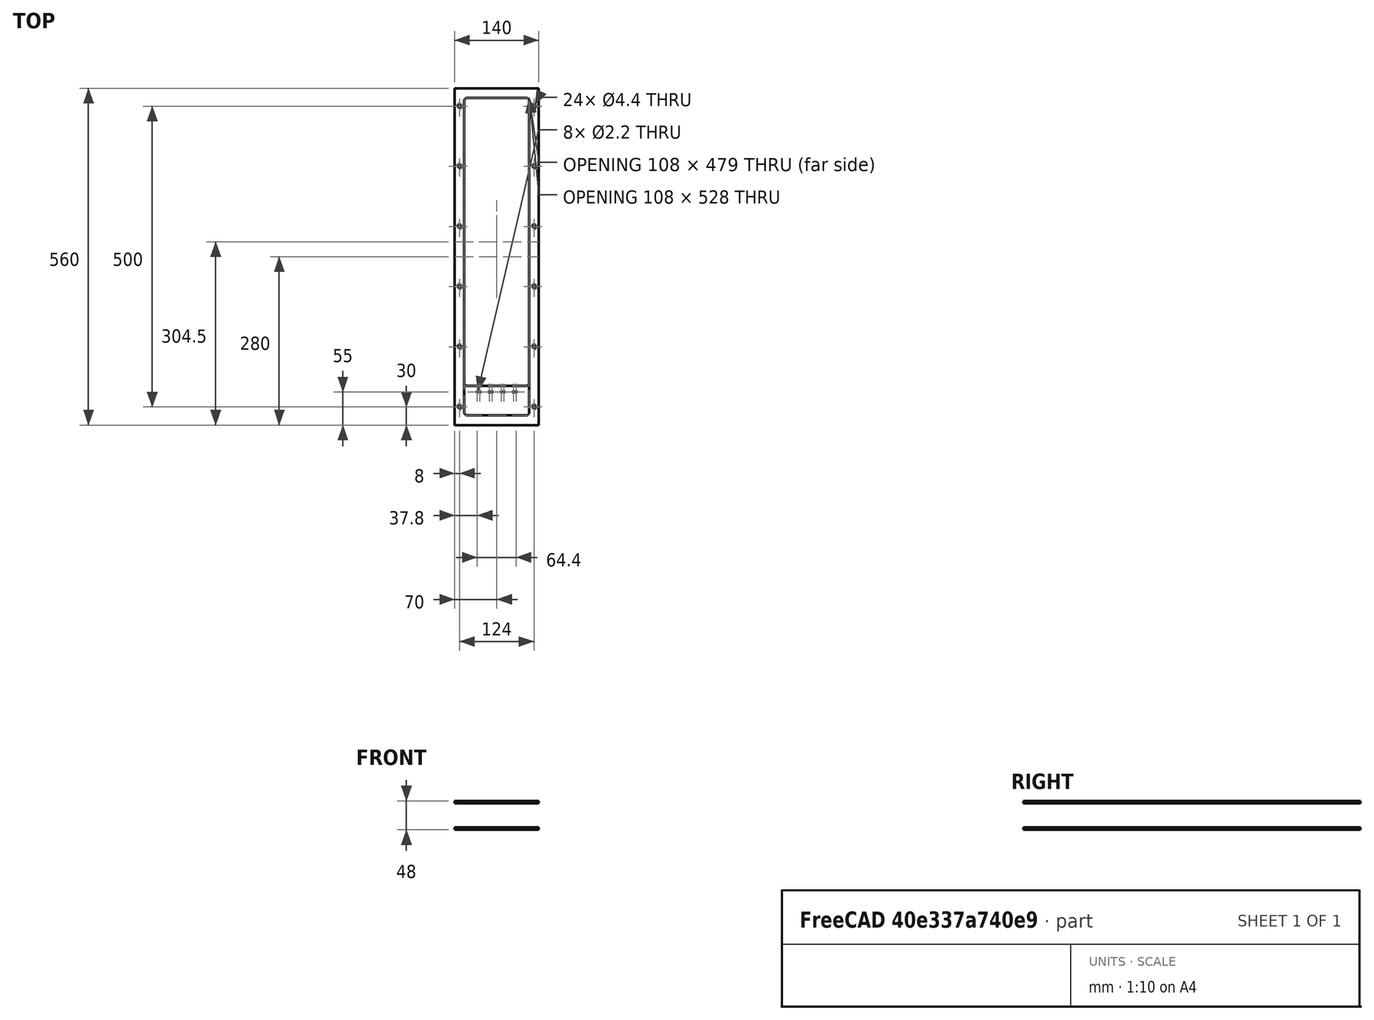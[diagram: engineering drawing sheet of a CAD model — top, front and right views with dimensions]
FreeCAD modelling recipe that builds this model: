
FCSTD DOCUMENT  (FreeCAD 0.20R29177 +233 (Git))
Label: carrier_plate_v1-0-560
License: All rights reserved
LicenseURL: http://en.wikipedia.org/wiki/All_rights_reserved
objects: TechDraw::DrawViewDimension×24, Sketcher::SketchObject×6, PartDesign::Pocket×4, PartDesign::Body×4, PartDesign::Pad×3, TechDraw::DrawViewBalloon×3, PartDesign::LinearPattern×2, PartDesign::FeatureBase×2, TechDraw::DrawViewPart×2, Spreadsheet::Sheet×1, TechDraw::DrawSVGTemplate×1, PartDesign::Chamfer×1, Part::Refine×1, PartDesign::Mirrored×1, TechDraw::DrawPage×1
note: 32 computed .brp shape members not serialized (recipe doc carries the construction recipe); baked Part::Feature solids carry a one-line shape summary decoded from their .brp

FEATURE [Sketcher::SketchObject] Sketch
  FullyConstrained = true
  MapMode = 5
  Support = -> [XY_Plane]
  expr: Constraints[10] = <<parameters>>.baseplate_length
  expr: Constraints[27] = <<parameters>>.side_width
  expr: Constraints[28] = <<parameters>>.side_width
  expr: Constraints[41] = <<parameters>>.cooling_fin_x_shift
  expr: Constraints[9] = <<parameters>>.baseplate_width
  sketch-geometry (20):
    g0: LineSegment StartX=-70 StartY=0 StartZ=0 EndX=70 EndY=0 EndZ=0
    g1: LineSegment StartX=70 StartY=0 StartZ=0 EndX=70 EndY=560 EndZ=0
    g2: LineSegment StartX=70 StartY=560 StartZ=0 EndX=-70 EndY=560 EndZ=0
    g3: LineSegment StartX=-70 StartY=560 StartZ=0 EndX=-70 EndY=0 EndZ=0
    g4: LineSegment StartX=-49 StartY=544 StartZ=0 EndX=49 EndY=544 EndZ=0
    g5: LineSegment StartX=54 StartY=539 StartZ=0 EndX=54 EndY=70 EndZ=0
    g6: LineSegment StartX=49 StartY=65 StartZ=0 EndX=-49 EndY=65 EndZ=0
    g7: LineSegment StartX=-54 StartY=70 StartZ=0 EndX=-54 EndY=539 EndZ=0
    g8: ArcOfCircle CenterX=49 CenterY=539 CenterZ=0 NormalX=0 NormalY=0 NormalZ=1 AngleXU=0 Radius=5 StartAngle=-3.0065e-12 EndAngle=1.5708
    g9: ArcOfCircle CenterX=-49 CenterY=539 CenterZ=0 NormalX=0 NormalY=0 NormalZ=1 AngleXU=0 Radius=5 StartAngle=1.5708 EndAngle=3.14159
    g10: ArcOfCircle CenterX=49 CenterY=70 CenterZ=0 NormalX=0 NormalY=0 NormalZ=1 AngleXU=0 Radius=5 StartAngle=4.71239 EndAngle=6.28319
    g11: ArcOfCircle CenterX=-49 CenterY=70 CenterZ=0 NormalX=0 NormalY=0 NormalZ=1 AngleXU=0 Radius=5 StartAngle=3.14159 EndAngle=4.71239
    g12: LineSegment StartX=-42.19 StartY=42 StartZ=0 EndX=59.31 EndY=42 EndZ=0
    g13: LineSegment StartX=59.31 StartY=42 StartZ=0 EndX=59.31 EndY=59 EndZ=0
    g14: LineSegment StartX=59.31 StartY=59 StartZ=0 EndX=-42.19 EndY=59 EndZ=0
    g15: LineSegment StartX=-42.19 StartY=59 StartZ=0 EndX=-42.19 EndY=42 EndZ=0
    g16: GeomPoint X=8.56 Y=50.5 Z=0
    g17: Circle CenterX=-22.19 CenterY=45 CenterZ=0 NormalX=0 NormalY=0 NormalZ=1 AngleXU=0 Radius=1.5
    g18: Circle CenterX=37.81 CenterY=45 CenterZ=0 NormalX=0 NormalY=0 NormalZ=1 AngleXU=0 Radius=1.5
    g19: LineSegment StartX=-22.19 StartY=45 StartZ=0 EndX=37.81 EndY=45 EndZ=0
  constraints (52):
    c: Coincident(g0,g1)
    c: Coincident(g1,g2)
    c: Coincident(g2,g3)
    c: Coincident(g3,g0)
    c: Horizontal(g0)
    c: Horizontal(g2)
    c: Vertical(g1)
    c: Vertical(g3)
    c: Symmetric(g0,g0,g-1)
    c: DistanceX(g0,g0) = 140
    c: DistanceY(g3,g3) = 560
    c: Horizontal(g6)
    c: Vertical(g5)
    c: Vertical(g7)
    c: Tangent(g5,g8) = 1.5708
    c: Tangent(g4,g8) = 1.5708
    c: Tangent(g7,g9) = 1.5708
    c: Tangent(g4,g9) = 1.5708
    c: Tangent(g6,g10) = 1.5708
    c: Tangent(g5,g10) = 1.5708
    c: Tangent(g6,g11) = 1.5708
    c: Tangent(g7,g11) = 1.5708
    c: Equal(g10,g11)
    c: Equal(g11,g8)
    c: Equal(g8,g9)
    c: Radius(g8) = 5
    c: Symmetric(g9,g8,g-2)
    c: DistanceY(g4,g1) = 16
    c: DistanceX(g5,g1) = 16
    c: DistanceY(g0,g6) = 65
    c: Coincident(g12,g13)
    c: Coincident(g13,g14)
    c: Coincident(g14,g15)
    c: Coincident(g15,g12)
    c: Horizontal(g12)
    c: Horizontal(g14)
    c: Vertical(g13)
    c: Vertical(g15)
    c: DistanceY(g13,g13) = 17
    c: Symmetric(g14,g12,g16)
    c: DistanceX(g12,g12) = 101.5
    c: DistanceX(g-1,g16) = 8.56
    c: Coincident(g19,g17)
    c: Coincident(g19,g18)
    c: Horizontal(g19)
    c: Equal(g18,g17)
    c: Diameter(g18) = 3
    c: DistanceY(g12,g17) = 3
    c: DistanceY(g0,g12) = 42
    c: DistanceX(g19,g19) = 60
    c: DistanceX(g12,g17) = 20
    c: DistanceY(g12,g6) = 23
FEATURE [PartDesign::Pad] Pad
  Direction = (0,0,1)
  Length = 4
  Length2 = 100
  Profile = -> Sketch
  Reversed = true
  Type = 0
  expr: Length = <<parameters>>.baseplate_thickness
FEATURE [Spreadsheet::Sheet] Spreadsheet  label="parameters"
  cells = B1=frame dimnsions:; B2=baseplate width; C2(baseplate_width)==140mm; D2=cooling fin x shift; E2(cooling_fin_x_shift)==8.56mm; B3=baseplate length; C3(baseplate_length)==560mm; D3=plate space; E3(plate_space)==40mm; B4=side width; C4(side_width)==16mm; B5=baseplate thickness; C5(baseplate_thickness)==4mm; B6=frame holes:; B7=hole step; C7(hole_step)==100mm; B8=hole offset; C8(hole_offset)==30mm
FEATURE [Sketcher::SketchObject] Sketch001
  FullyConstrained = true
  MapMode = 5
  Support = -> [Pad]
  expr: Constraints[3] = <<parameters>>.baseplate_width - <<parameters>>.side_width
  sketch-geometry (2):
    g0: Circle CenterX=62 CenterY=30 CenterZ=0 NormalX=0 NormalY=0 NormalZ=1 AngleXU=0 Radius=2.2
    g1: Circle CenterX=-62 CenterY=30 CenterZ=0 NormalX=0 NormalY=0 NormalZ=1 AngleXU=0 Radius=2.2
  constraints (5):
    c: Symmetric(g1,g0,g-2)
    c: Equal(g1,g0)
    c: Diameter(g0) = 4.4
    c: DistanceX(g1,g0) = 124
    c: DistanceY(g-1,g0) = 30
FEATURE [PartDesign::Pocket] Pocket
  BaseFeature = -> Pad
  Direction = (0,0,-1)
  Length = 5
  Length2 = 100
  Profile = -> Sketch001
  Type = 1
FEATURE [PartDesign::LinearPattern] LinearPattern
  BaseFeature = -> Pocket
  Direction = -> Y_Axis
  Length = 500
  Occurrences = 6
  Originals = -> [Pocket]
  expr: Length = <<parameters>>.baseplate_length - <<parameters>>.hole_offset * 2
  expr: Occurrences = Length / <<parameters>>.hole_step + 1
FEATURE [Sketcher::SketchObject] Sketch002
  FullyConstrained = true
  MapMode = 5
  Support = -> [XY_Plane001]
  expr: Constraints[10] = <<parameters>>.baseplate_length
  expr: Constraints[27] = <<parameters>>.side_width
  expr: Constraints[28] = <<parameters>>.side_width
  expr: Constraints[29] = <<parameters>>.side_width
  expr: Constraints[9] = <<parameters>>.baseplate_width
  sketch-geometry (12):
    g0: LineSegment StartX=-70 StartY=0 StartZ=0 EndX=70 EndY=0 EndZ=0
    g1: LineSegment StartX=70 StartY=0 StartZ=0 EndX=70 EndY=560 EndZ=0
    g2: LineSegment StartX=70 StartY=560 StartZ=0 EndX=-70 EndY=560 EndZ=0
    g3: LineSegment StartX=-70 StartY=560 StartZ=0 EndX=-70 EndY=0 EndZ=0
    g4: LineSegment StartX=-49 StartY=544 StartZ=0 EndX=49 EndY=544 EndZ=0
    g5: LineSegment StartX=54 StartY=539 StartZ=0 EndX=54 EndY=21 EndZ=0
    g6: LineSegment StartX=49 StartY=16 StartZ=0 EndX=-49 EndY=16 EndZ=0
    g7: LineSegment StartX=-54 StartY=21 StartZ=0 EndX=-54 EndY=539 EndZ=0
    g8: ArcOfCircle CenterX=49 CenterY=539 CenterZ=0 NormalX=0 NormalY=0 NormalZ=1 AngleXU=0 Radius=5 StartAngle=1.1e-15 EndAngle=1.5708
    g9: ArcOfCircle CenterX=-49 CenterY=539 CenterZ=0 NormalX=0 NormalY=0 NormalZ=1 AngleXU=0 Radius=5 StartAngle=1.5708 EndAngle=3.14159
    g10: ArcOfCircle CenterX=49 CenterY=21 CenterZ=0 NormalX=0 NormalY=0 NormalZ=1 AngleXU=0 Radius=5 StartAngle=4.71239 EndAngle=6.28319
    g11: ArcOfCircle CenterX=-49 CenterY=21 CenterZ=0 NormalX=0 NormalY=0 NormalZ=1 AngleXU=0 Radius=5 StartAngle=3.14159 EndAngle=4.71239
  constraints (30):
    c: Coincident(g0,g1)
    c: Coincident(g1,g2)
    c: Coincident(g2,g3)
    c: Coincident(g3,g0)
    c: Horizontal(g0)
    c: Horizontal(g2)
    c: Vertical(g1)
    c: Vertical(g3)
    c: Symmetric(g0,g0,g-1)
    c: DistanceX(g0,g0) = 140
    c: DistanceY(g3,g3) = 560
    c: Horizontal(g6)
    c: Vertical(g5)
    c: Vertical(g7)
    c: Tangent(g5,g8) = 1.5708
    c: Tangent(g4,g8) = 1.5708
    c: Tangent(g7,g9) = 1.5708
    c: Tangent(g4,g9) = 1.5708
    c: Tangent(g6,g10) = 1.5708
    c: Tangent(g5,g10) = 1.5708
    c: Tangent(g6,g11) = 1.5708
    c: Tangent(g7,g11) = 1.5708
    c: Equal(g11,g10)
    c: Equal(g10,g8)
    c: Equal(g8,g9)
    c: Radius(g8) = 5
    c: Symmetric(g5,g7,g-2)
    c: DistanceY(g4,g1) = 16
    c: DistanceX(g5,g1) = 16
    c: DistanceY(g0,g6) = 16
FEATURE [PartDesign::Pad] Pad001
  Direction = (0,0,1)
  Length = 4
  Length2 = 100
  Profile = -> Sketch002
  Type = 0
  expr: Length = <<parameters>>.baseplate_thickness
FEATURE [Sketcher::SketchObject] Sketch003
  FullyConstrained = true
  MapMode = 5
  Placement = pos=(0,0,4) rot=(0,0,1;0rad)
  Support = -> [Pad001]
  expr: Constraints[3] = <<parameters>>.baseplate_width - <<parameters>>.side_width
  expr: Constraints[4] = <<parameters>>.hole_offset
  sketch-geometry (2):
    g0: Circle CenterX=62 CenterY=30 CenterZ=0 NormalX=0 NormalY=0 NormalZ=1 AngleXU=0 Radius=2.2
    g1: Circle CenterX=-62 CenterY=30 CenterZ=0 NormalX=0 NormalY=0 NormalZ=1 AngleXU=0 Radius=2.2
  constraints (5):
    c: Symmetric(g1,g0,g-2)
    c: Equal(g0,g1)
    c: Diameter(g0) = 4.4
    c: DistanceX(g1,g0) = 124
    c: DistanceY(g-1,g1) = 30
FEATURE [PartDesign::Pocket] Pocket001
  BaseFeature = -> Pad001
  Direction = (1,1,1)
  Length = 5
  Length2 = 100
  Profile = -> Sketch003
  Type = 1
FEATURE [PartDesign::LinearPattern] LinearPattern001
  BaseFeature = -> Pocket001
  Direction = -> Y_Axis001
  Length = 500
  Occurrences = 6
  Originals = -> [Pocket001]
  expr: Length = <<parameters>>.baseplate_length - 2 * <<parameters>>.hole_offset
  expr: Occurrences = Length / <<parameters>>.hole_step + 1
FEATURE [PartDesign::Body] Body001  label="top_plate"
  Group = -> [Sketch002,Pad001,Sketch003,Pocket001,LinearPattern001]
  Origin = -> Origin001
  Placement = pos=(0,0,40) rot=(0,0,1;0rad)
  Tip = -> LinearPattern001
  expr: .Placement.Base.z = <<parameters>>.plate_space
FEATURE [TechDraw::DrawSVGTemplate] Template
  Height = 297
  Orientation = 1
  Width = 420
FEATURE [Sketcher::SketchObject] Sketch004
  FullyConstrained = true
  MapMode = 5
  Support = -> [LinearPattern]
  sketch-geometry (8):
    g0: LineSegment StartX=-44 StartY=14 StartZ=0 EndX=44 EndY=14 EndZ=0
    g1: LineSegment StartX=44 StartY=14 StartZ=0 EndX=44 EndY=36 EndZ=0
    g2: LineSegment StartX=44 StartY=36 StartZ=0 EndX=-44 EndY=36 EndZ=0
    g3: LineSegment StartX=-44 StartY=36 StartZ=0 EndX=-44 EndY=14 EndZ=0
    g4: Circle CenterX=44 CenterY=36 CenterZ=0 NormalX=0 NormalY=0 NormalZ=1 AngleXU=0 Radius=1.6
    g5: Circle CenterX=-44 CenterY=36 CenterZ=0 NormalX=0 NormalY=0 NormalZ=1 AngleXU=0 Radius=1.6
    g6: Circle CenterX=-44 CenterY=14 CenterZ=0 NormalX=0 NormalY=0 NormalZ=1 AngleXU=0 Radius=1.6
    g7: Circle CenterX=44 CenterY=14 CenterZ=0 NormalX=0 NormalY=0 NormalZ=1 AngleXU=0 Radius=1.6
  constraints (19):
    c: Coincident(g0,g1)
    c: Coincident(g1,g2)
    c: Coincident(g2,g3)
    c: Coincident(g3,g0)
    c: Horizontal(g0)
    c: Vertical(g1)
    c: Vertical(g3)
    c: Symmetric(g1,g2,g-2)
    c: Coincident(g4,g1)
    c: Coincident(g5,g2)
    c: Coincident(g6,g0)
    c: Coincident(g7,g0)
    c: Equal(g7,g4)
    c: Equal(g4,g6)
    c: Equal(g6,g5)
    c: Diameter(g5) = 3.2
    c: DistanceY(g3,g3) = 22
    c: DistanceX(g0,g0) = 88
    c: DistanceY(g7) = 14
FEATURE [PartDesign::Pocket] Pocket002
  BaseFeature = -> LinearPattern
  Direction = (0,0,-1)
  Length = 5
  Length2 = 100
  Profile = -> Sketch004
  Type = 1
FEATURE [PartDesign::Body] Body  label="bottom_plate"
  Group = -> [Sketch,Pad,Sketch001,Pocket,LinearPattern,Sketch004,Pocket002]
  Origin = -> Origin
  Tip = -> Pocket002
FEATURE [PartDesign::FeatureBase] Clone
  BaseFeature = -> Body
FEATURE [PartDesign::Pad] Pad002
  BaseFeature = -> Clone
  Direction = (0,0,1)
  Length = 4
  Length2 = 10
  Profile = -> Clone [Edge19,Edge20,Edge18,Edge16,Edge14,Edge13]
  Reversed = true
  Type = 0
FEATURE [PartDesign::Chamfer] Chamfer
  Angle = 45
  Base = -> Pad002 [Edge48,Edge39,Edge42,Edge49,Edge50,Edge44,Edge51,Edge62,Edge63,Edge52,Edge53,Edge64]
  BaseFeature = -> Pad002
  ChamferType = 0
  FlipDirection = false
  Size = 2.5
  Size2 = 1
  SupportTransform = false
  UseAllEdges = false
FEATURE [PartDesign::Body] Body002
  BaseFeature = -> Body
  Group = -> [Clone,Pad002,Chamfer]
  Origin = -> Origin002
  Tip = -> Chamfer
FEATURE [Part::Refine] Body002001
  Source = -> Body002
FEATURE [PartDesign::FeatureBase] BaseFeature
  BaseFeature = -> Body002001
FEATURE [Sketcher::SketchObject] Sketch005
  FullyConstrained = true
  MapMode = 5
  Support = -> [BaseFeature]
  sketch-geometry (7):
    g0: Circle CenterX=-27.8 CenterY=55 CenterZ=0 NormalX=0 NormalY=0 NormalZ=1 AngleXU=0 Radius=1.1
    g1: Circle CenterX=-7.8 CenterY=55 CenterZ=0 NormalX=0 NormalY=0 NormalZ=1 AngleXU=0 Radius=1.1
    g2: LineSegment StartX=-27.8 StartY=55 StartZ=0 EndX=-7.8 EndY=55 EndZ=0
    g3: Circle CenterX=12.2 CenterY=55 CenterZ=0 NormalX=0 NormalY=0 NormalZ=1 AngleXU=0 Radius=1.1
    g4: LineSegment StartX=-7.8 StartY=55 StartZ=0 EndX=12.2 EndY=55 EndZ=0
    g5: Circle CenterX=32.2 CenterY=55 CenterZ=0 NormalX=0 NormalY=0 NormalZ=1 AngleXU=0 Radius=1.1
    g6: LineSegment StartX=12.2 StartY=55 StartZ=0 EndX=32.2 EndY=55 EndZ=0
  constraints (18):
    c: Coincident(g0,g2)
    c: Coincident(g1,g2)
    c: Distance(g2) = 20
    c: Coincident(g1,g4)
    c: Coincident(g3,g4)
    c: Equal(g2,g4)
    c: Parallel(g4,g2)
    c: Coincident(g3,g6)
    c: Coincident(g5,g6)
    c: Equal(g2,g6)
    c: Parallel(g6,g2)
    c: Horizontal(g4)
    c: Equal(g0,g1)
    c: Equal(g1,g3)
    c: Equal(g3,g5)
    c: Diameter(g0) = 2.2
    c: DistanceX(g3) = 12.2
    c: DistanceY(g5) = 55
FEATURE [PartDesign::Pocket] Pocket003
  BaseFeature = -> BaseFeature
  Direction = (0,0,-1)
  Length = 5
  Length2 = 5
  Profile = -> Sketch005
  ReferenceAxis = -> Sketch005 [N_Axis]
  Type = 1
FEATURE [PartDesign::Mirrored] Mirrored
  BaseFeature = -> Pocket003
  MirrorPlane = -> Sketch005 [V_Axis]
  Originals = -> [Pocket003]
FEATURE [PartDesign::Body] Body002002  label="bottom_plate_v2"
  BaseFeature = -> Body002001
  Group = -> [BaseFeature,Sketch005,Pocket003,Mirrored]
  Origin = -> Origin003
  Tip = -> Mirrored
FEATURE [TechDraw::DrawViewPart] View
  Caption = Bottom plate
  CoarseView = false
  Direction = (0,0,1)
  Focus = 100
  HardHidden = false
  IsoCount = 0
  IsoHidden = false
  IsoVisible = false
  LockPosition = false
  Perspective = false
  Rotation = 0
  Scale = 0.5
  ScaleType = 2
  SeamHidden = false
  SeamVisible = true
  SmoothHidden = false
  SmoothVisible = true
  Source = -> [Body002002]
  X = 224.888
  XDirection = (0,1,0)
  Y = 228.319
FEATURE [TechDraw::DrawViewPart] View001
  Caption = Top plate
  CoarseView = false
  Direction = (0,0,1)
  Focus = 100
  HardHidden = false
  IsoCount = 0
  IsoHidden = false
  IsoVisible = false
  LockPosition = false
  Perspective = false
  Rotation = 0
  Scale = 0.5
  ScaleType = 2
  SeamHidden = false
  SeamVisible = true
  SmoothHidden = false
  SmoothVisible = true
  Source = -> [Body001]
  X = 224.931
  XDirection = (0,1,0)
  Y = 117.85
FEATURE [TechDraw::DrawViewDimension] Dimension
  AngleOverride = false
  Arbitrary = false
  ArbitraryTolerances = false
  EqualTolerance = true
  ExtensionAngle = 0
  FormatSpec = ⌀%.2w
  FormatSpecOverTolerance = %+.2w
  FormatSpecUnderTolerance = %+.2w
  Inverted = false
  LineAngle = 0
  LockPosition = false
  MeasureType = 1
  OverTolerance = 0
  References2D = -> [View]
  Rotation = 0
  ScaleType = 0
  TheoreticalExact = false
  Type = 5
  UnderTolerance = 0
  X = 155.93
  Y = 53.8676
FEATURE [TechDraw::DrawViewBalloon] Balloon
  BubbleShape = 1
  EndType = 0
  EndTypeScale = 1
  KinkLength = 5
  LockPosition = false
  OriginX = 250
  OriginY = 64.2
  Rotation = 0
  ScaleType = 0
  ShapeScale = 1
  SourceView = -> View
  Text = 12 holes with 2.5mm chamfer
  TextWrapLen = -1
  X = 173.296
  Y = 10.1883
FEATURE [TechDraw::DrawViewBalloon] Balloon001
  BubbleShape = 1
  EndType = 0
  EndTypeScale = 1
  KinkLength = 5
  LockPosition = false
  OriginX = -225
  OriginY = 32.2
  Rotation = 0
  ScaleType = 0
  ShapeScale = 1
  SourceView = -> View
  Text = 8 holes M2.5
  TextWrapLen = -1
  X = -129.275
  Y = 7.95751
FEATURE [TechDraw::DrawViewDimension] Dimension001
  AngleOverride = false
  Arbitrary = false
  ArbitraryTolerances = false
  EqualTolerance = true
  ExtensionAngle = 0
  FormatSpec = %.2w
  FormatSpecOverTolerance = %+.2w
  FormatSpecUnderTolerance = %+.2w
  Inverted = false
  LineAngle = 0
  LockPosition = false
  MeasureType = 1
  OverTolerance = 0
  References2D = -> [View]
  Rotation = 0
  ScaleType = 0
  TheoreticalExact = false
  Type = 1
  UnderTolerance = 0
  X = -132.74
  Y = -169.591
FEATURE [TechDraw::DrawViewDimension] Dimension002
  AngleOverride = false
  Arbitrary = false
  ArbitraryTolerances = false
  EqualTolerance = true
  ExtensionAngle = 0
  FormatSpec = %.2w
  FormatSpecOverTolerance = %+.2w
  FormatSpecUnderTolerance = %+.2w
  Inverted = false
  LineAngle = 0
  LockPosition = false
  MeasureType = 1
  OverTolerance = 0
  References2D = -> [View]
  Rotation = 0
  ScaleType = 0
  TheoreticalExact = false
  Type = 1
  UnderTolerance = 0
  X = -125.864
  Y = 44.7876
FEATURE [TechDraw::DrawViewDimension] Dimension003
  AngleOverride = false
  Arbitrary = false
  ArbitraryTolerances = false
  EqualTolerance = true
  ExtensionAngle = 0
  FormatSpec = %.2w
  FormatSpecOverTolerance = %+.2w
  FormatSpecUnderTolerance = %+.2w
  Inverted = false
  LineAngle = 0
  LockPosition = false
  MeasureType = 1
  OverTolerance = 0
  References2D = -> [View]
  Rotation = 0
  ScaleType = 0
  TheoreticalExact = false
  Type = 1
  UnderTolerance = 0
  X = -112.093
  Y = -177.344
FEATURE [TechDraw::DrawViewDimension] Dimension004
  AngleOverride = false
  Arbitrary = false
  ArbitraryTolerances = false
  EqualTolerance = true
  ExtensionAngle = 0
  FormatSpec = %.2w
  FormatSpecOverTolerance = %+.2w
  FormatSpecUnderTolerance = %+.2w
  Inverted = false
  LineAngle = 0
  LockPosition = false
  MeasureType = 1
  OverTolerance = 0
  References2D = -> [View]
  Rotation = 0
  ScaleType = 0
  TheoreticalExact = false
  Type = 1
  UnderTolerance = 0
  X = -78.1776
  Y = -185.425
FEATURE [TechDraw::DrawViewDimension] Dimension005
  AngleOverride = false
  Arbitrary = false
  ArbitraryTolerances = false
  EqualTolerance = true
  ExtensionAngle = 0
  FormatSpec = %.2w
  FormatSpecOverTolerance = %+.2w
  FormatSpecUnderTolerance = %+.2w
  Inverted = false
  LineAngle = 0
  LockPosition = false
  MeasureType = 1
  OverTolerance = 0
  References2D = -> [View]
  Rotation = 0
  ScaleType = 0
  TheoreticalExact = false
  Type = 1
  UnderTolerance = 0
  X = -51.0164
  Y = -192.155
FEATURE [TechDraw::DrawViewDimension] Dimension006
  AngleOverride = false
  Arbitrary = false
  ArbitraryTolerances = false
  EqualTolerance = true
  ExtensionAngle = 0
  FormatSpec = %.2w
  FormatSpecOverTolerance = %+.2w
  FormatSpecUnderTolerance = %+.2w
  Inverted = false
  LineAngle = 0
  LockPosition = false
  MeasureType = 1
  OverTolerance = 0
  References2D = -> [View]
  Rotation = 0
  ScaleType = 0
  TheoreticalExact = false
  Type = 1
  UnderTolerance = 0
  X = -30.609
  Y = -198.615
FEATURE [TechDraw::DrawViewDimension] Dimension007
  AngleOverride = false
  Arbitrary = false
  ArbitraryTolerances = false
  EqualTolerance = true
  ExtensionAngle = 0
  FormatSpec = %.2w
  FormatSpecOverTolerance = %+.2w
  FormatSpecUnderTolerance = %+.2w
  Inverted = false
  LineAngle = 0
  LockPosition = false
  MeasureType = 1
  OverTolerance = 0
  References2D = -> [View]
  Rotation = 0
  ScaleType = 0
  TheoreticalExact = false
  Type = 1
  UnderTolerance = 0
  X = -5.33881
  Y = -206.835
FEATURE [TechDraw::DrawViewDimension] Dimension008
  AngleOverride = false
  Arbitrary = false
  ArbitraryTolerances = false
  EqualTolerance = true
  ExtensionAngle = 0
  FormatSpec = %.2w
  FormatSpecOverTolerance = %+.2w
  FormatSpecUnderTolerance = %+.2w
  Inverted = false
  LineAngle = 0
  LockPosition = false
  MeasureType = 1
  OverTolerance = 0
  References2D = -> [View001]
  Rotation = 0
  ScaleType = 0
  TheoreticalExact = false
  Type = 1
  UnderTolerance = 0
  X = -1.84486
  Y = 164.34
FEATURE [TechDraw::DrawViewDimension] Dimension017
  AngleOverride = false
  Arbitrary = false
  ArbitraryTolerances = false
  EqualTolerance = true
  ExtensionAngle = 0
  FormatSpec = %.2w
  FormatSpecOverTolerance = %+.2w
  FormatSpecUnderTolerance = %+.2w
  Inverted = false
  LineAngle = 0
  LockPosition = false
  MeasureType = 1
  OverTolerance = 0
  References2D = -> [View001]
  Rotation = 0
  ScaleType = 0
  TheoreticalExact = false
  Type = 2
  UnderTolerance = 0
  X = 165.286
  Y = 1.52747
FEATURE [TechDraw::DrawViewBalloon] Balloon002
  BubbleShape = 1
  EndType = 0
  EndTypeScale = 1
  KinkLength = 5
  LockPosition = false
  OriginX = 250
  OriginY = 64.2
  Rotation = 0
  ScaleType = 0
  ShapeScale = 1
  SourceView = -> View001
  Text = 12 holes with 2.5mm chamfer
  TextWrapLen = -1
  X = 173.311
  Y = 18.6529
FEATURE [TechDraw::DrawViewDimension] Dimension018
  AngleOverride = false
  Arbitrary = false
  ArbitraryTolerances = false
  EqualTolerance = true
  ExtensionAngle = 0
  FormatSpec = ⌀%.2w
  FormatSpecOverTolerance = %+.2w
  FormatSpecUnderTolerance = %+.2w
  Inverted = false
  LineAngle = 0
  LockPosition = false
  MeasureType = 1
  OverTolerance = 0
  References2D = -> [View001]
  Rotation = 0
  ScaleType = 0
  TheoreticalExact = false
  Type = 5
  UnderTolerance = 0
  X = 157.704
  Y = 54.1423
FEATURE [TechDraw::DrawViewDimension] Dimension019
  AngleOverride = false
  Arbitrary = false
  ArbitraryTolerances = false
  EqualTolerance = true
  ExtensionAngle = 0
  FormatSpec = %.2w
  FormatSpecOverTolerance = %+.2w
  FormatSpecUnderTolerance = %+.2w
  Inverted = false
  LineAngle = 0
  LockPosition = false
  MeasureType = 1
  OverTolerance = 0
  References2D = -> [View]
  Rotation = 0
  ScaleType = 0
  TheoreticalExact = false
  Type = 2
  UnderTolerance = 0
  X = 146.674
  Y = -40.6702
FEATURE [TechDraw::DrawViewDimension] Dimension020
  AngleOverride = false
  Arbitrary = false
  ArbitraryTolerances = false
  EqualTolerance = true
  ExtensionAngle = 0
  FormatSpec = %.2w
  FormatSpecOverTolerance = %+.2w
  FormatSpecUnderTolerance = %+.2w
  Inverted = false
  LineAngle = 0
  LockPosition = false
  MeasureType = 1
  OverTolerance = 0
  References2D = -> [View]
  Rotation = 0
  ScaleType = 0
  TheoreticalExact = false
  Type = 2
  UnderTolerance = 0
  X = 154
  Y = 0.5
FEATURE [TechDraw::DrawViewDimension] Dimension021
  AngleOverride = false
  Arbitrary = false
  ArbitraryTolerances = false
  EqualTolerance = true
  ExtensionAngle = 0
  FormatSpec = %.2w
  FormatSpecOverTolerance = %+.2w
  FormatSpecUnderTolerance = %+.2w
  Inverted = false
  LineAngle = 0
  LockPosition = false
  MeasureType = 1
  OverTolerance = 0
  References2D = -> [View001]
  Rotation = 0
  ScaleType = 0
  TheoreticalExact = false
  Type = 2
  UnderTolerance = 0
  X = 147.355
  Y = -40.0882
FEATURE [TechDraw::DrawViewDimension] Dimension022
  AngleOverride = false
  Arbitrary = false
  ArbitraryTolerances = false
  EqualTolerance = true
  ExtensionAngle = 0
  FormatSpec = %.2w
  FormatSpecOverTolerance = %+.2w
  FormatSpecUnderTolerance = %+.2w
  Inverted = false
  LineAngle = 0
  LockPosition = false
  MeasureType = 1
  OverTolerance = 0
  References2D = -> [View001]
  Rotation = 0
  ScaleType = 0
  TheoreticalExact = false
  Type = 2
  UnderTolerance = 0
  X = 154
  Y = 0.5
FEATURE [TechDraw::DrawViewDimension] Dimension023
  AngleOverride = false
  Arbitrary = false
  ArbitraryTolerances = false
  EqualTolerance = true
  ExtensionAngle = 0
  FormatSpec = %.2w
  FormatSpecOverTolerance = %+.2w
  FormatSpecUnderTolerance = %+.2w
  Inverted = false
  LineAngle = 0
  LockPosition = false
  MeasureType = 1
  OverTolerance = 0
  References2D = -> [View]
  Rotation = 0
  ScaleType = 0
  TheoreticalExact = false
  Type = 2
  UnderTolerance = 0
  X = 164.661
  Y = 0.527114
FEATURE [TechDraw::DrawViewDimension] Dimension024
  AngleOverride = false
  Arbitrary = false
  ArbitraryTolerances = false
  EqualTolerance = true
  ExtensionAngle = 0
  FormatSpec = %.2w
  FormatSpecOverTolerance = %+.2w
  FormatSpecUnderTolerance = %+.2w
  Inverted = false
  LineAngle = 0
  LockPosition = false
  MeasureType = 1
  OverTolerance = 0
  References2D = -> [View]
  Rotation = 0
  ScaleType = 0
  TheoreticalExact = false
  Type = 2
  UnderTolerance = 0
  X = -145.581
  Y = -22.5219
FEATURE [TechDraw::DrawViewDimension] Dimension025
  AngleOverride = false
  Arbitrary = false
  ArbitraryTolerances = false
  EqualTolerance = true
  ExtensionAngle = 0
  FormatSpec = %.2w
  FormatSpecOverTolerance = %+.2w
  FormatSpecUnderTolerance = %+.2w
  Inverted = false
  LineAngle = 0
  LockPosition = false
  MeasureType = 1
  OverTolerance = 0
  References2D = -> [View]
  Rotation = 0
  ScaleType = 0
  TheoreticalExact = false
  Type = 2
  UnderTolerance = 0
  X = -153.484
  Y = -19.6493
FEATURE [TechDraw::DrawViewDimension] Dimension026
  AngleOverride = false
  Arbitrary = false
  ArbitraryTolerances = false
  EqualTolerance = true
  ExtensionAngle = 0
  FormatSpec = %.2w
  FormatSpecOverTolerance = %+.2w
  FormatSpecUnderTolerance = %+.2w
  Inverted = false
  LineAngle = 0
  LockPosition = false
  MeasureType = 1
  OverTolerance = 0
  References2D = -> [View]
  Rotation = 0
  ScaleType = 0
  TheoreticalExact = false
  Type = 2
  UnderTolerance = 0
  X = -160.116
  Y = -17.4671
FEATURE [TechDraw::DrawViewDimension] Dimension027
  AngleOverride = false
  Arbitrary = false
  ArbitraryTolerances = false
  EqualTolerance = true
  ExtensionAngle = 0
  FormatSpec = %.2w
  FormatSpecOverTolerance = %+.2w
  FormatSpecUnderTolerance = %+.2w
  Inverted = false
  LineAngle = 0
  LockPosition = false
  MeasureType = 1
  OverTolerance = 0
  References2D = -> [View]
  Rotation = 0
  ScaleType = 0
  TheoreticalExact = false
  Type = 2
  UnderTolerance = 0
  X = -167.407
  Y = -16.95
FEATURE [TechDraw::DrawViewDimension] Dimension028
  AngleOverride = false
  Arbitrary = false
  ArbitraryTolerances = false
  EqualTolerance = true
  ExtensionAngle = 0
  FormatSpec = %.2w
  FormatSpecOverTolerance = %+.2w
  FormatSpecUnderTolerance = %+.2w
  Inverted = false
  LineAngle = 0
  LockPosition = false
  MeasureType = 1
  OverTolerance = 0
  References2D = -> [View]
  Rotation = 0
  ScaleType = 0
  TheoreticalExact = false
  Type = 2
  UnderTolerance = 0
  X = -175.573
  Y = -12.1756
FEATURE [TechDraw::DrawViewDimension] Dimension029
  AngleOverride = false
  Arbitrary = false
  ArbitraryTolerances = false
  EqualTolerance = true
  ExtensionAngle = 0
  FormatSpec = %.2w
  FormatSpecOverTolerance = %+.2w
  FormatSpecUnderTolerance = %+.2w
  Inverted = false
  LineAngle = 0
  LockPosition = false
  MeasureType = 1
  OverTolerance = 0
  References2D = -> [View]
  Rotation = 0
  ScaleType = 0
  TheoreticalExact = false
  Type = 2
  UnderTolerance = 0
  X = -184.03
  Y = -11.6585
FEATURE [TechDraw::DrawViewDimension] Dimension030
  AngleOverride = false
  Arbitrary = false
  ArbitraryTolerances = false
  EqualTolerance = true
  ExtensionAngle = 0
  FormatSpec = %.2w
  FormatSpecOverTolerance = %+.2w
  FormatSpecUnderTolerance = %+.2w
  Inverted = false
  LineAngle = 0
  LockPosition = false
  MeasureType = 1
  OverTolerance = 0
  References2D = -> [View]
  Rotation = 0
  ScaleType = 0
  TheoreticalExact = false
  Type = 2
  UnderTolerance = 0
  X = -192.779
  Y = -6.88415
FEATURE [TechDraw::DrawViewDimension] Dimension031
  AngleOverride = false
  Arbitrary = false
  ArbitraryTolerances = false
  EqualTolerance = true
  ExtensionAngle = 0
  FormatSpec = %.2w
  FormatSpecOverTolerance = %+.2w
  FormatSpecUnderTolerance = %+.2w
  Inverted = false
  LineAngle = 0
  LockPosition = false
  MeasureType = 1
  OverTolerance = 0
  References2D = -> [View]
  Rotation = 0
  ScaleType = 0
  TheoreticalExact = false
  Type = 2
  UnderTolerance = 0
  X = -200.945
  Y = -5.20123
FEATURE [TechDraw::DrawPage] Page
  KeepUpdated = true
  NextBalloonIndex = 4
  ProjectionType = 0
  Template = -> Template
  Views = -> [View,View001,Dimension,Balloon,Balloon001,Dimension001,Dimension002,Dimension003,Dimension004,Dimension005,Dimension006,Dimension007,Dimension008,Dimension017,Balloon002,Dimension018,Dimension019,Dimension020,Dimension021,Dimension022,Dimension023,Dimension024,Dimension025,Dimension026,Dimension027,Dimension028,Dimension029,Dimension030,Dimension031]
